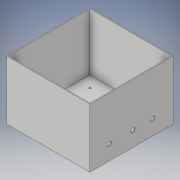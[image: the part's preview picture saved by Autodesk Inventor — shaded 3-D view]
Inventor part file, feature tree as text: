
AUTODESK INVENTOR PART (.ipt)
format: ipt  version: 2018 (Build 220112000, 112)  size: 152,576 bytes
history: native  units: in
note: dims shown in document units (in); Inventor stores cm internally (conversion verified against a paired STEP export)
features: sketch x7, extrude x6
ambient origin geometry x8: Origin, YZ Plane, XZ Plane, XY Plane, X Axis, Y Axis, Z Axis, Center Point
bodies: Solid1 (feature_tree)
feature tree (13):
  extrude  "Extrusion1"  Depth=4.76in
  extrude  "Extrusion2"  Depth=4.66in
  extrude  "Extrusion3"  Depth=3.26in TaperAngle=0.0deg
  extrude  "Extrusion4"  Depth=0.164in
  extrude  "Extrusion5"  Depth=2.598in
  sketch  "Sketch6"  dims[d15=0.787in d16=0.118in]
  extrude  "Extrusion6"  Depth=0.118in
  sketch  "Sketch1"  dims[d0=4.76in d1=4.76in]
  sketch  "Sketch2"  dims[d2=0.1in d3=0.0in d4=4.66in]
  sketch  "Sketch3"  dims[d5=4.66in d6=3.26in d7=0.0in]
  sketch  "Sketch4"  dims[d10=0.164in d11=0.164in]
  sketch  "Sketch5"  dims[d12=0.0in d13=0.0in d14=2.598in]
  sketch  "Sketch7"  dims[d17=0.118in d18=0.118in d19=0.118in d20=3.937in d21=3.937in d28=0.112in d29=0.112in d30=0.112in d31=0.112in d32=0.0in d33=0.0in d34=0.25in d35=1.0in d36=0.0in d40=0.25in d41=0.25in d42=0.25in d43=0.0in d44=0.0in]
